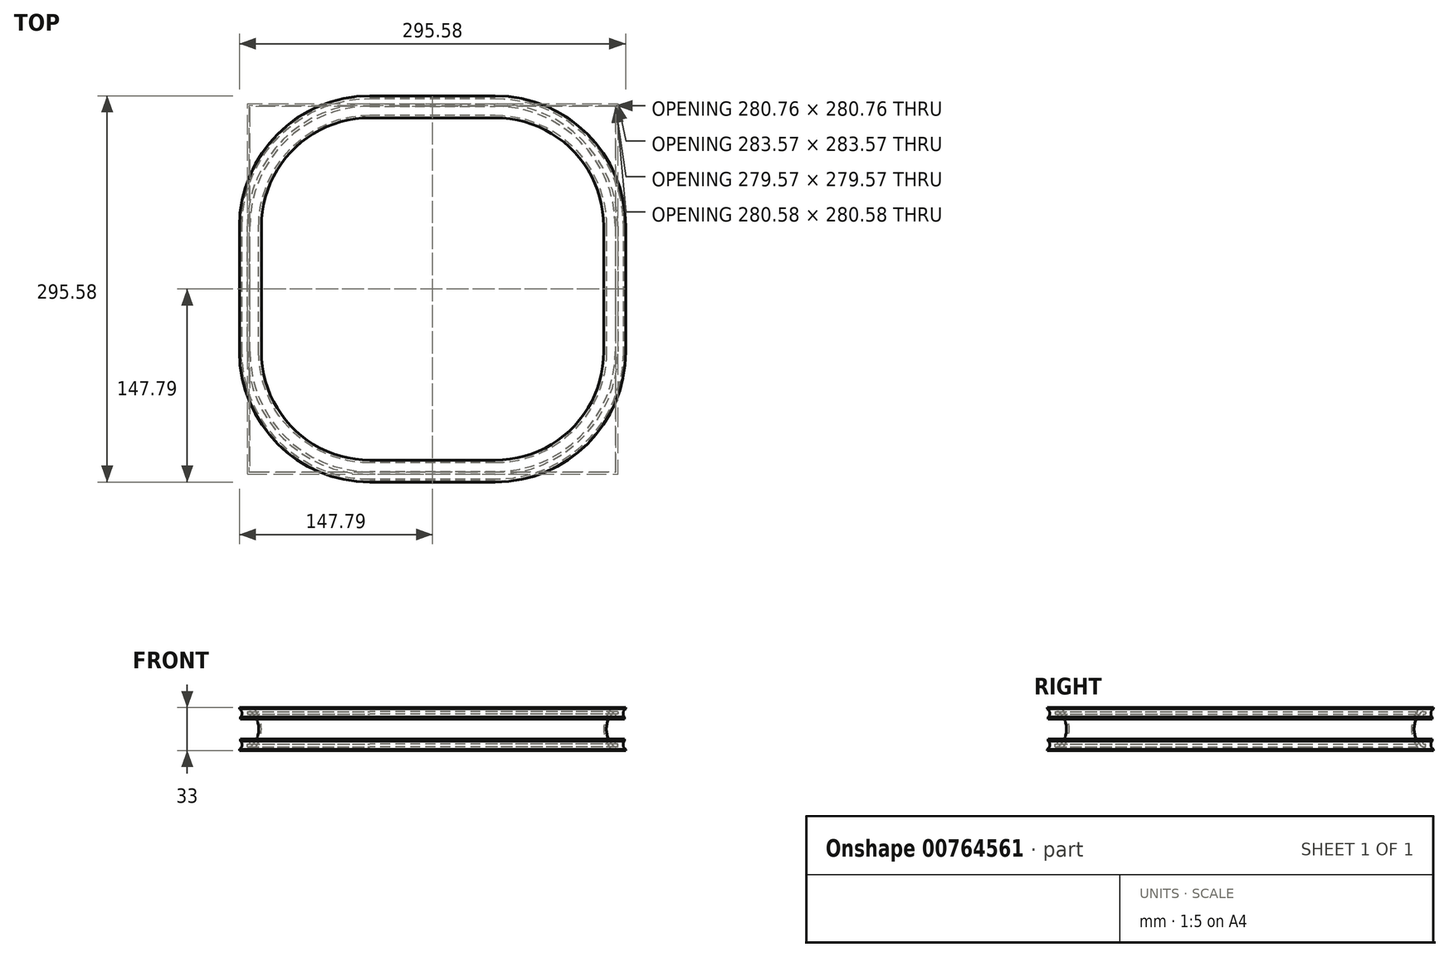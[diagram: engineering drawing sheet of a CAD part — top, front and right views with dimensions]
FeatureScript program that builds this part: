
annotation { "Feature Type Name" : "Feature", "Feature Type Description" : "" }
export const myFeature = defineFeature(function(context is Context, id is Id, definition is map)
    precondition{}
    {
        {
            var Q0;
            Q0=qCreatedBy(makeId("Top.planeOp"),FACE);
            var sketch = newSketch(context, id + "F0", { "sketchPlane" : qUnion([Q0])});
            skLineSegment(sketch, "E0.bottom", {"start": v(-48, 148) * mm, "end": v(48, 148) * mm});
            skLineSegment(sketch, "E0.top", {"start": v(-48, -148) * mm, "end": v(48, -148) * mm});
            skLineSegment(sketch, "E0.left", {"start": v(-148, 48) * mm, "end": v(-148, -48) * mm});
            skLineSegment(sketch, "E0.right", {"start": v(148, 48) * mm, "end": v(148, -48) * mm});
            skPoint(sketch, "E1.visualSharp", {"position": v(148, 148) * mm});
            skArc(sketch, "E1.filletArc", {"start": v(148, 48) * mm, "mid": v(118.71, 118.71) * mm, "end": v(48, 148) * mm});
            skPoint(sketch, "E2.visualSharp", {"position": v(148, -148) * mm});
            skArc(sketch, "E2.filletArc", {"start": v(48, -148) * mm, "mid": v(118.71, -118.71) * mm, "end": v(148, -48) * mm});
            skPoint(sketch, "E3.visualSharp", {"position": v(-148, -148) * mm});
            skArc(sketch, "E3.filletArc", {"start": v(-148, -48) * mm, "mid": v(-118.71, -118.71) * mm, "end": v(-48, -148) * mm});
            skPoint(sketch, "E4.visualSharp", {"position": v(-148, 148) * mm});
            skArc(sketch, "E4.filletArc", {"start": v(-48, 148) * mm, "mid": v(-118.71, 118.71) * mm, "end": v(-148, 48) * mm});
            skLineSegment(sketch, "E5.bottom", {"start": v(-158, 158) * mm, "end": v(158, 158) * mm});
            skLineSegment(sketch, "E5.top", {"start": v(-158, -158) * mm, "end": v(158, -158) * mm});
            skLineSegment(sketch, "E5.left", {"start": v(-158, 158) * mm, "end": v(-158, -158) * mm});
            skLineSegment(sketch, "E5.right", {"start": v(158, 158) * mm, "end": v(158, -158) * mm});
            skPoint(sketch, "E6.visualSharp", {"position": v(-132, -132) * mm});
            skArc(sketch, "E7.0", {"start": v(-132, -48) * mm, "mid": v(-107.4, -107.4) * mm, "end": v(-48, -132) * mm});
            skLineSegment(sketch, "E8.0", {"start": v(-132, 48) * mm, "end": v(-132, -48) * mm});
            skArc(sketch, "E9.MirrorCS", {"start": v(-132, 48) * mm, "mid": v(-107.4, 107.4) * mm, "end": v(-48, 132) * mm});
            skLineSegment(sketch, "E10.0", {"start": v(-48, -132) * mm, "end": v(48, -132) * mm});
            skArc(sketch, "E11.0", {"start": v(48, -132) * mm, "mid": v(107.4, -107.4) * mm, "end": v(132, -48) * mm});
            skLineSegment(sketch, "E12.0", {"start": v(132, 48) * mm, "end": v(132, -48) * mm});
            skArc(sketch, "E13.0", {"start": v(132, 48) * mm, "mid": v(107.4, 107.4) * mm, "end": v(48, 132) * mm});
            skLineSegment(sketch, "E14.0", {"start": v(-48, 132) * mm, "end": v(48, 132) * mm});
            skSolve(sketch);
        }
        {
            var Q0;
            Q0=qCreatedBy(makeId("Right.planeOp"),FACE);
            var sketch = newSketch(context, id + "F1", { "sketchPlane" : qUnion([Q0])});
            skArc(sketch, "E15", {"start": v(131, 0) * mm, "mid": v(132.15, -7.35) * mm, "end": v(135.5, -14) * mm});
            skArc(sketch, "E16", {"start": v(133, 0) * mm, "mid": v(134.34, -6.8) * mm, "end": v(138.15, -12.6) * mm});
            skLineSegment(sketch, "E17", {"start": v(190.4, 0) * mm, "end": v(151, 0) * mm, "construction": true});
            skLineSegment(sketch, "E18", {"start": v(133, 0) * mm, "end": v(133, -32.44) * mm, "construction": true});
            skLineSegment(sketch, "E19", {"start": v(131, 0) * mm, "end": v(131, -29.3) * mm, "construction": true});
            skLineSegment(sketch, "E20", {"start": v(140.38, -16.5) * mm, "end": v(146.79, -16.5) * mm});
            skPoint(sketch, "E21.orphan", {"position": v(196.82, 16.5) * mm});
            skPoint(sketch, "E22.orphan", {"position": v(120.62, -16.5) * mm});
            skPoint(sketch, "E23.visualSharp", {"position": v(137.57, -16.5) * mm});
            skArc(sketch, "E23.filletArc", {"start": v(135.5, -14) * mm, "mid": v(137.64, -15.84) * mm, "end": v(140.38, -16.5) * mm});
            skLineSegment(sketch, "E24", {"start": v(141.79, -13.5) * mm, "end": v(140.29, -13.5) * mm});
            skPoint(sketch, "E25.visualSharp", {"position": v(139.1, -13.5) * mm});
            skArc(sketch, "E25.filletArc", {"start": v(138.15, -12.6) * mm, "mid": v(139.13, -13.27) * mm, "end": v(140.29, -13.5) * mm});
            skLineSegment(sketch, "E26", {"start": v(146.79, -16.5) * mm, "end": v(147.79, -16.5) * mm});
            skLineSegment(sketch, "E27", {"start": v(147.79, -16.5) * mm, "end": v(147.79, -15.46) * mm});
            skLineSegment(sketch, "E28", {"start": v(147, -7.5) * mm, "end": v(141.79, -7.5) * mm});
            skLineSegment(sketch, "E29", {"start": v(141.79, -13.5) * mm, "end": v(141.79, -11.5) * mm});
            skLineSegment(sketch, "E30", {"start": v(139.79, -9.5) * mm, "end": v(141.79, -7.5) * mm});
            skLineSegment(sketch, "E31", {"start": v(141.79, -11.5) * mm, "end": v(139.79, -11.5) * mm});
            skLineSegment(sketch, "E32", {"start": v(139.79, -11.5) * mm, "end": v(139.79, -9.5) * mm});
            skLineSegment(sketch, "E33", {"start": v(145.79, -33.1) * mm, "end": v(145.79, -39.25) * mm, "construction": true});
            skLineSegment(sketch, "E34", {"start": v(147.79, -12) * mm, "end": v(241.75, -12) * mm, "construction": true});
            skArc(sketch, "E35", {"start": v(147, -9.13) * mm, "mid": v(145.82, -12.5) * mm, "end": v(147.79, -15.46) * mm});
            skPoint(sketch, "E36.orphan", {"position": v(147.79, -7.5) * mm});
            skArc(sketch, "E37.MirrorCS", {"start": v(138.15, -12.6) * mm, "mid": v(134.34, -6.8) * mm, "end": v(133, 0) * mm});
            skLineSegment(sketch, "E38.trimOffspring", {"start": v(147, -7.5) * mm, "end": v(147, -9.13) * mm});
            skLineSegment(sketch, "E39.trimOffspring", {"start": v(147, -9.13) * mm, "end": v(147, -7.5) * mm});
            skPoint(sketch, "E40.MirrorCS.start.orphan", {"position": v(225.42, -41.06) * mm});
            skLineSegment(sketch, "E41.MirrorCS", {"start": v(147, 9.13) * mm, "end": v(147, 7.5) * mm});
            skLineSegment(sketch, "E42.MirrorCS", {"start": v(139.79, 11.5) * mm, "end": v(139.79, 9.5) * mm});
            skLineSegment(sketch, "E43.MirrorCS", {"start": v(147, 7.5) * mm, "end": v(147, 9.13) * mm});
            skArc(sketch, "E44.MirrorCS", {"start": v(138.15, 12.6) * mm, "mid": v(139.13, 13.27) * mm, "end": v(140.29, 13.5) * mm});
            skLineSegment(sketch, "E45.MirrorCS", {"start": v(141.79, 11.5) * mm, "end": v(139.79, 11.5) * mm});
            skLineSegment(sketch, "E46.MirrorCS", {"start": v(141.79, 13.5) * mm, "end": v(140.29, 13.5) * mm});
            skLineSegment(sketch, "E47.MirrorCS", {"start": v(141.79, 13.5) * mm, "end": v(141.79, 11.5) * mm});
            skLineSegment(sketch, "E48.MirrorCS", {"start": v(147.79, 16.5) * mm, "end": v(147.79, 15.46) * mm});
            skLineSegment(sketch, "E49.MirrorCS", {"start": v(146.79, 16.5) * mm, "end": v(147.79, 16.5) * mm});
            skLineSegment(sketch, "E50.MirrorCS", {"start": v(139.79, 9.5) * mm, "end": v(141.79, 7.5) * mm});
            skArc(sketch, "E51.MirrorCS", {"start": v(135.5, 14) * mm, "mid": v(137.64, 15.84) * mm, "end": v(140.38, 16.5) * mm});
            skArc(sketch, "E52.MirrorCS", {"start": v(138.15, 12.6) * mm, "mid": v(134.34, 6.8) * mm, "end": v(133, 0) * mm});
            skPoint(sketch, "E53.MirrorP", {"position": v(120.62, 16.5) * mm});
            skLineSegment(sketch, "E54.MirrorCS", {"start": v(147.79, 12) * mm, "end": v(241.75, 12) * mm, "construction": true});
            skArc(sketch, "E55.MirrorCS", {"start": v(147, 9.13) * mm, "mid": v(145.82, 12.5) * mm, "end": v(147.79, 15.46) * mm});
            skPoint(sketch, "E56.MirrorP", {"position": v(225.42, 41.06) * mm});
            skPoint(sketch, "E57.MirrorP", {"position": v(137.57, 16.5) * mm});
            skLineSegment(sketch, "E58.MirrorCS", {"start": v(133, 0) * mm, "end": v(133, 32.44) * mm, "construction": true});
            skPoint(sketch, "E59.MirrorP", {"position": v(147.79, 7.5) * mm});
            skPoint(sketch, "E60.MirrorP", {"position": v(139.1, 13.5) * mm});
            skLineSegment(sketch, "E61.MirrorCS", {"start": v(131, 0) * mm, "end": v(131, 29.3) * mm, "construction": true});
            skArc(sketch, "E62.MirrorCS", {"start": v(131, 0) * mm, "mid": v(132.15, 7.35) * mm, "end": v(135.5, 14) * mm});
            skLineSegment(sketch, "E63.MirrorCS", {"start": v(145.79, 33.1) * mm, "end": v(145.79, 39.25) * mm, "construction": true});
            skArc(sketch, "E64.MirrorCS", {"start": v(133, 0) * mm, "mid": v(134.34, 6.8) * mm, "end": v(138.15, 12.6) * mm});
            skLineSegment(sketch, "E65.MirrorCS", {"start": v(140.38, 16.5) * mm, "end": v(146.79, 16.5) * mm});
            skLineSegment(sketch, "E66.MirrorCS", {"start": v(147, 7.5) * mm, "end": v(141.79, 7.5) * mm});
            skSolve(sketch);
        }
        {
            var Q0;
            Q0 = qSketchRegion(id + "F1", true);
            var Q1;
            Q1=sQuery(id+"F0.wireOp",EDGE,"E14.0");
            var Q2;
            Q2=sQuery(id+"F0.wireOp",EDGE,"E9.MirrorCS");
            var Q3;
            Q3=sQuery(id+"F0.wireOp",EDGE,"E8.0");
            var Q4;
            Q4=sQuery(id+"F0.wireOp",EDGE,"E7.0");
            var Q5;
            Q5=sQuery(id+"F0.wireOp",EDGE,"E10.0");
            var Q6;
            Q6=sQuery(id+"F0.wireOp",EDGE,"E11.0");
            var Q7;
            Q7=sQuery(id+"F0.wireOp",EDGE,"E12.0");
            var Q8;
            Q8=sQuery(id+"F0.wireOp",EDGE,"E13.0");
            sweep(context, id + "F2", {"profiles" : qUnion([Q0]), "path" : qUnion([Q1, Q2, Q3, Q4, Q5, Q6, Q7, Q8])});
        }
    });
